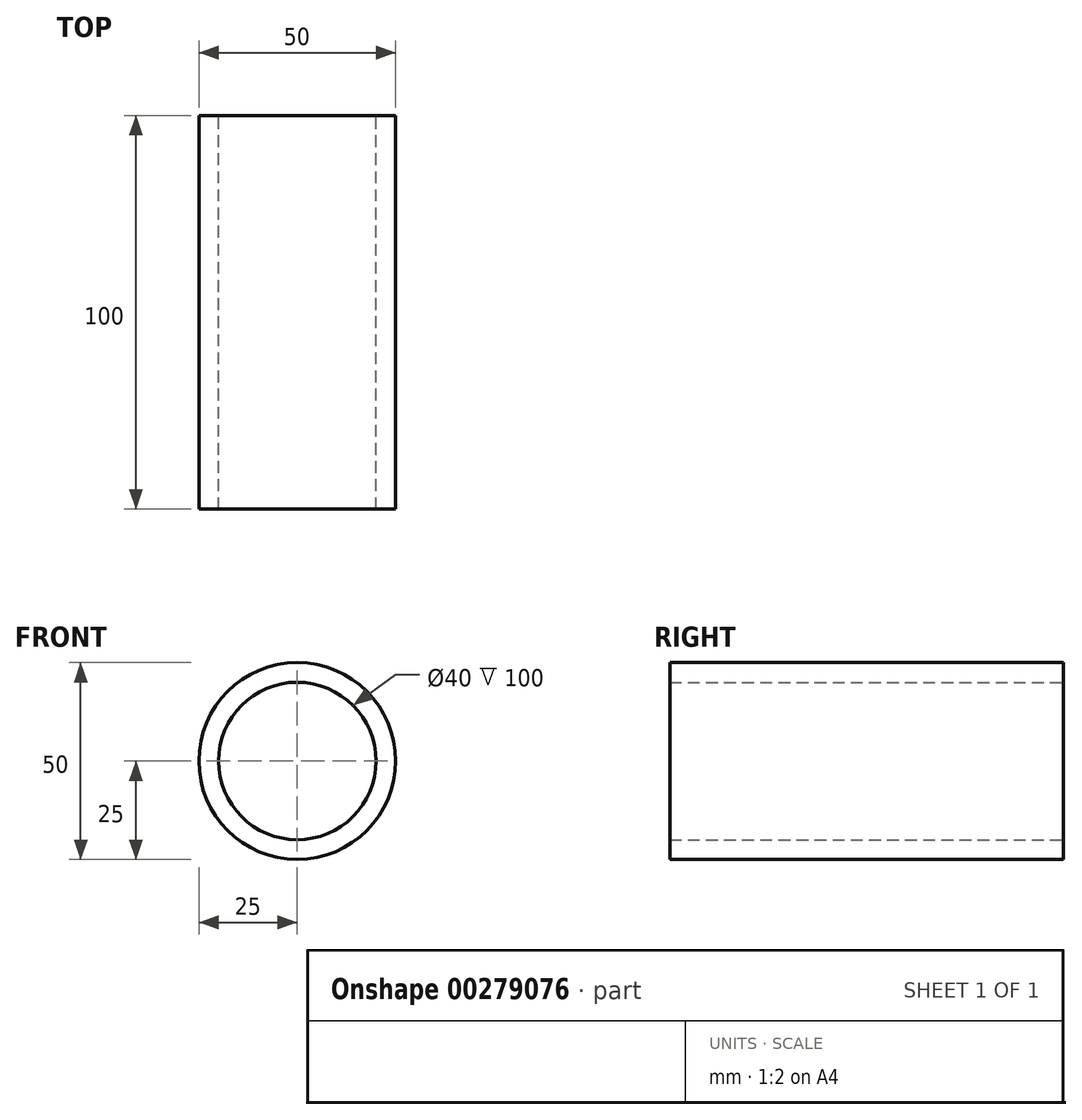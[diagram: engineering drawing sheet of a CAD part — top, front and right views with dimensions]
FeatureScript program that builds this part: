
annotation { "Feature Type Name" : "Feature", "Feature Type Description" : "" }
export const myFeature = defineFeature(function(context is Context, id is Id, definition is map)
    precondition{}
    {
        {
            var Q0;
            Q0=qCreatedBy(makeId("Front.planeOp"),FACE);
            var sketch = newSketch(context, id + "F0", { "sketchPlane" : qUnion([Q0])});
            skCircle(sketch, "E0", {"center": v(0, 0) * mm, "radius": 25 * mm});
            skCircle(sketch, "E1", {"center": v(0, 0) * mm, "radius": 20 * mm});
            skSolve(sketch);
        }
        {
            var Q0;
            Q0 = qSketchRegion(id + "F0", true);
            extrude(context, id + "F1", {"entities" : qUnion([Q0]), "depth" : 50 * mm, "hasSecondDirection" : true, "secondDirectionOppositeDirection" : true, "secondDirectionDepth" : 50 * mm});
        }
    });
